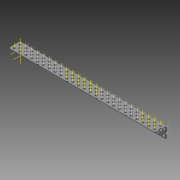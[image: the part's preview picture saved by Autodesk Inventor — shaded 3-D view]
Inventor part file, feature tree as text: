
AUTODESK INVENTOR PART (.ipt)
format: ipt  version: 2015 (Build 190159000, 159)  size: 2,272,256 bytes
history: native  units: in
note: dims shown in document units (in); Inventor stores cm internally (conversion verified against a paired STEP export)
features: other x155, pattern_linear x4, sheet_metal_op x1, extrude x1, imported_body x1, sketch x1
ambient origin geometry x8: Origin, YZ Plane, XZ Plane, XY Plane, X Axis, Y Axis, Z Axis, Center Point
bodies: Body1 (feature_tree)
feature tree (163):
  sheet_metal_op  "Fold1"
  other  "L-Channel"
  extrude  "length cut"  Depth=0.5in
  other  "top out axis"
  other  "top inner axis"
  other  "back out axis"
  other  "back inner axis"
  pattern_linear  "top outer axes"  Count1=2 Spacing1=0.5in
  pattern_linear  "top inner axes"  Spacing1=0.5in  [1 undecoded]
  pattern_linear  "back outer axes"  Count1=2 Spacing1=0.5in
  pattern_linear  "back inner axes"  Spacing1=0.5in  [1 undecoded]
  other  "right plane"
  imported_body  "Base1"
  sketch  "Sketch1"  dims[d1=0.0in d4=0.5in d5=0.7874in d7=0.5in d10=0.5in d13=0.5in d14=0.7874in d16=0.5in d19=0.5in d20=-12.5in d21=0.0in d22=0.0in d23=0.0in d24=0.0in d25=0.0in d26=0.0in]
  other  "Work Point1"
  other  "Work Point2"
  other  "Work Point3"
  other  "Work Point4"
  other  "Work Axis5"
  other  "Work Axis6"
  other  "Work Axis7"
  other  "Work Axis8"
  other  "Work Axis11"
  other  "Work Axis12"
  other  "Work Axis13"
  other  "Work Axis14"
  other  "Work Axis15"
  other  "Work Axis18"
  other  "Work Axis19"
  other  "Work Axis20"
  other  "Work Axis23"
  other  "Work Axis24"
  other  "Work Axis25"
  other  "Work Axis26"
  other  "Work Axis29"
  other  "Work Axis30"
  other  "Work Axis31"
  other  "Work Axis32"
  other  "Work Axis33"
  other  "Work Axis36"
  other  "Work Axis37"
  other  "Work Axis38"
  other  "Work Axis41"
  other  "Work Axis42"
  other  "Work Axis43"
  other  "Work Axis44"
  other  "Work Axis45"
  other  "Work Axis46"
  other  "Work Axis47"
  other  "Work Axis48"
  other  "Work Axis49"
  other  "Work Axis50"
  other  "Work Axis51"
  other  "Work Axis52"
  other  "Work Axis53"
  other  "Work Axis54"
  other  "Work Axis55"
  other  "Work Axis56"
  other  "Work Axis57"
  other  "Work Axis58"
  other  "Work Axis59"
  other  "Work Axis60"
  other  "Work Axis61"
  other  "Work Axis62"
  other  "Work Axis63"
  other  "Work Axis64"
  other  "Work Axis65"
  other  "Work Axis66"
  other  "Work Axis67"
  other  "Work Axis68"
  other  "Work Axis69"
  other  "Work Axis70"
  other  "Work Axis71"
  other  "Work Axis72"
  other  "Work Axis73"
  other  "Work Axis74"
  other  "Work Axis75"
  other  "Work Axis76"
  other  "Work Axis77"
  other  "Work Axis78"
  other  "Work Axis79"
  other  "Work Axis80"
  other  "Work Axis81"
  other  "Work Axis82"
  other  "Work Axis83"
  other  "Work Axis84"
  other  "Work Axis85"
  other  "Work Axis86"
  other  "Work Axis87"
  other  "Work Axis88"
  other  "Work Axis89"
  other  "Work Axis90"
  other  "Work Axis91"
  other  "Work Axis92"
  other  "Work Axis93"
  other  "Work Axis94"
  other  "Work Axis95"
  other  "Work Axis96"
  other  "Work Axis97"
  other  "Work Axis98"
  other  "Work Axis99"
  other  "Work Axis100"
  other  "Work Axis101"
  other  "Work Axis102"
  other  "Work Axis103"
  other  "Work Axis104"
  other  "Work Axis105"
  other  "Work Axis106"
  other  "Work Axis107"
  other  "Work Axis108"
  other  "Work Axis109"
  other  "Work Axis110"
  other  "Work Axis111"
  other  "Work Axis112"
  other  "Work Axis113"
  other  "Work Axis114"
  other  "Work Axis115"
  other  "Work Axis116"
  other  "Work Axis117"
  other  "Work Axis118"
  other  "Work Axis119"
  other  "Work Axis120"
  other  "Work Axis121"
  other  "Work Axis122"
  other  "Work Axis123"
  other  "Work Axis124"
  other  "Work Axis125"
  other  "Work Axis126"
  other  "Work Axis127"
  other  "Work Axis128"
  other  "Work Axis129"
  other  "Work Axis130"
  other  "Work Axis131"
  other  "Work Axis132"
  other  "Work Axis133"
  other  "Work Axis134"
  other  "Work Axis135"
  other  "Work Axis136"
  other  "Work Axis137"
  other  "Work Axis138"
  other  "Work Axis139"
  other  "Work Axis140"
  other  "Work Axis141"
  other  "Work Axis142"
  other  "Work Axis143"
  other  "Work Axis144"
  other  "Work Axis145"
  other  "Work Axis146"
  other  "Work Axis147"
  other  "Work Axis148"
  other  "Work Axis149"
  other  "Work Axis150"
  other  "Work Axis151"
  other  "Work Axis152"
  other  "Work Axis153"
  other  "Work Axis154"
  other  "Work Axis155"
  other  "Work Axis156"
  other  "Work Axis157"
  other  "Work Axis158"
  other  "Work Axis159"
  other  "Work Axis160"
  other  "left plane"
note: 2 required parameter values undecoded (feature->parameter linkage not recoverable at this tier; creation-order binding heuristic only, values carry confidence <= 0.55)
